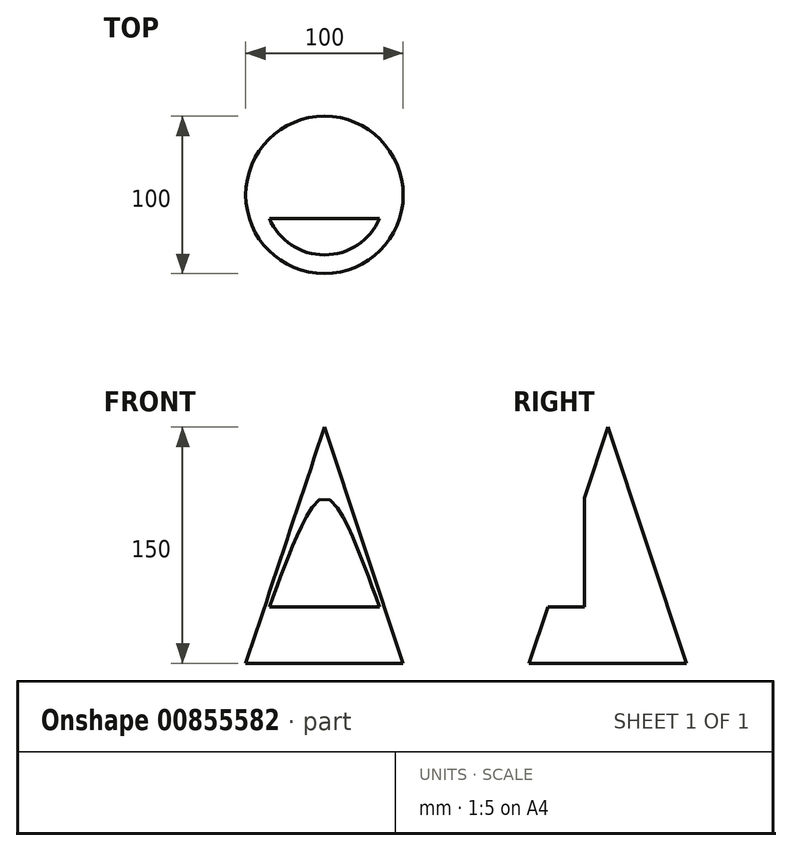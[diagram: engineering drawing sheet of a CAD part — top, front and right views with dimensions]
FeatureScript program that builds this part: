
annotation { "Feature Type Name" : "Feature", "Feature Type Description" : "" }
export const myFeature = defineFeature(function(context is Context, id is Id, definition is map)
    precondition{}
    {
        {
            var Q0;
            Q0=qCreatedBy(makeId("Front.planeOp"),FACE);
            var sketch = newSketch(context, id + "F0", { "sketchPlane" : qUnion([Q0])});
            skLineSegment(sketch, "E0", {"start": v(0, 150) * mm, "end": v(0, -91.14) * mm, "construction": true});
            skLineSegment(sketch, "E1", {"start": v(0, 150) * mm, "end": v(50, 0) * mm});
            skLineSegment(sketch, "E2", {"start": v(0, 0) * mm, "end": v(50, 0) * mm});
            skLineSegment(sketch, "E3", {"start": v(0, 150) * mm, "end": v(0, 0) * mm});
            skSolve(sketch);
        }
        {
            var Q0;
            Q0=makeQuery(id+"F0.imprint","IMPRINT",FACE,{"disambiguationData":[TD([[makeQuery(id+"F0.imprint","IMPRINT",EDGE,{"derivedFrom":sQuery(id+"F0.wireOp",EDGE,"E1")}),-1.0]])]});
            var Q1;
            Q1=sQuery(id+"F0.wireOp",EDGE,"E0");
            revolve(context, id + "F1", {"surfaceOperationType" : NewSurfaceOperationType.NEW, "entities" : qUnion([Q0]), "axis" : qUnion([Q1]), "revolveType" : RevolveType.FULL});
        }
        {
            var Q0;
            Q0=qCreatedBy(makeId("Front.planeOp"),FACE);
            var sketch = newSketch(context, id + "F2", { "sketchPlane" : qUnion([Q0])});
            skLineSegment(sketch, "E4.bottom", {"start": v(53.25, 112.92) * mm, "end": v(-59.3, 112.92) * mm});
            skLineSegment(sketch, "E4.top", {"start": v(53.25, 35.71) * mm, "end": v(-59.3, 35.71) * mm});
            skLineSegment(sketch, "E4.left", {"start": v(53.25, 112.92) * mm, "end": v(53.25, 35.71) * mm});
            skLineSegment(sketch, "E4.right", {"start": v(-59.3, 112.92) * mm, "end": v(-59.3, 35.71) * mm});
            skSolve(sketch);
        }
        {
            var Q0;
            Q0=makeQuery(id+"F2.imprint","IMPRINT",FACE,{"disambiguationData":[TD([[makeQuery(id+"F2.imprint","IMPRINT",EDGE,{"derivedFrom":sQuery(id+"F2.wireOp",EDGE,"E4.bottom")}),1.0]])]});
            extrude(context, id + "F3", {"entities" : qUnion([Q0]), "operationType" : NewBodyOperationType.REMOVE, "endBound" : BoundingType.THROUGH_ALL, "depth" : 25 * mm, "offsetDistance" : 25 * mm, "hasSecondDirection" : true, "secondDirectionOppositeDirection" : false, "secondDirectionDepth" : 15 * mm});
        }
    });
